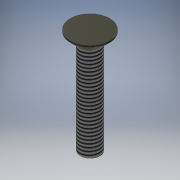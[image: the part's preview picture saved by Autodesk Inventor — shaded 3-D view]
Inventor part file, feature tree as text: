
AUTODESK INVENTOR PART (.ipt)
format: ipt  version: 2016 (Build 200138000, 138)  size: 134,656 bytes
history: native  units: mm
features: extrude x5, sketch x5, other x1, thread x1, chamfer x1
ambient origin geometry x1: Origin
bodies: Body1 (feature_tree)
feature tree (13):
  other  "ソリッド1"
  extrude  "押し出し1"  Depth=3.0mm
  extrude  "押し出し2"  Depth=6.0mm TaperAngle=0.0deg
  thread  "ねじ1"
  chamfer  "面取り1"  Distance=6.0mm
  extrude  "押し出し4"  Depth=1.75mm TaperAngle=0.0deg
  extrude  "押し出し5"  Depth=10.0mm TaperAngle=0.0deg
  extrude  "押し出し6"  Depth=1.5mm TaperAngle=45.0deg
  sketch  "スケッチ1"
  sketch  "スケッチ2"
  sketch  "スケッチ4"
  sketch  "スケッチ5"
  sketch  "スケッチ6"
